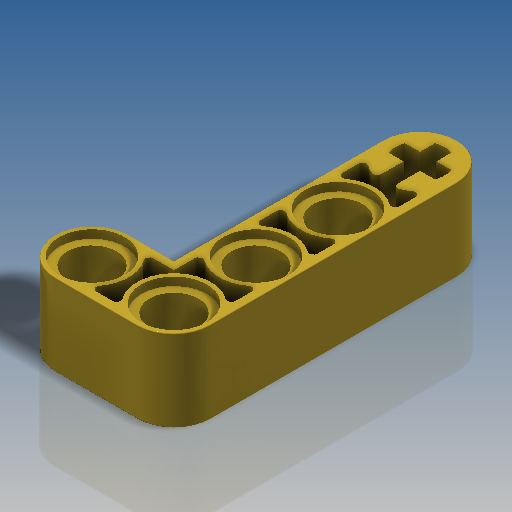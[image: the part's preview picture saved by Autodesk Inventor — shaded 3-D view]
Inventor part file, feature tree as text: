
AUTODESK INVENTOR PART (.ipt)
format: ipt  version: 2018.3 (Build 223284000, 284)  size: 366,592 bytes
history: native  units: mm
features: extrude x3, sketch x2, mirror x1, fillet x1
ambient origin geometry x8: Origin, YZ Plane, XZ Plane, XY Plane, X Axis, Y Axis, Z Axis, Center Point
bodies: Solid1 (feature_tree)
feature tree (7):
  extrude  "Extrusion1"  Depth=6.4mm
  sketch  "Sketch6"  dims[d14=8.0mm d15=0.0mm d32=7.2mm d34=8.0mm d36=0.8mm d41=0.8mm d42=0.0mm d43=3.1mm d44=0.0mm d46=0.4mm d47=0.1mm d48=1.6mm d49=0.8mm]
  extrude  "Extrusion7"  Depth=7.2mm
  extrude  "Extrusion8"  Depth=8.0mm
  mirror  "Mirror1"
  fillet  "Fillet1"  Radius=0.8mm
  sketch  "Sketch1"  dims[d8=4.8mm d9=6.4mm]
